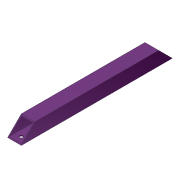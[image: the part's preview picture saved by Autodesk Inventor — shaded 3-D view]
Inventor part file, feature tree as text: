
AUTODESK INVENTOR PART (.ipt)
format: ipt  version: 2012 (Build 160160000, 160)  size: 107,008 bytes
history: native  units: in
note: dims shown in document units (in); Inventor stores cm internally (conversion verified against a paired STEP export)
features: extrude x4, sketch x4, shell x1
ambient origin geometry x8: Origin, YZ Plane, XZ Plane, XY Plane, X Axis, Y Axis, Z Axis, Center Point
bodies: Solid1 (feature_tree)
feature tree (9):
  extrude  "Extrusion1"  Depth=1.0in
  shell  "Shell1"  Thickness=11.0in
  extrude  "Extrusion2"  Depth=1.0in
  extrude  "Extrusion3"  Depth=11.0in TaperAngle=0.0deg
  extrude  "Extrusion4"  Depth=0.5in
  sketch  "Sketch1"  dims[d0=1.0in d1=1.0in d2=11.0in d3=0.0in]
  sketch  "Sketch2"  dims[d4=0.0625in d5=1.0in]
  sketch  "Sketch3"  dims[d6=1.0in d7=11.0in d8=0.0in]
  sketch  "Sketch4"  dims[d9=0.25in d10=0.5in d11=0.5in d12=0.5in d13=0.5in d14=11.0in d15=0.0in d16=11.0in d17=0.0in]
